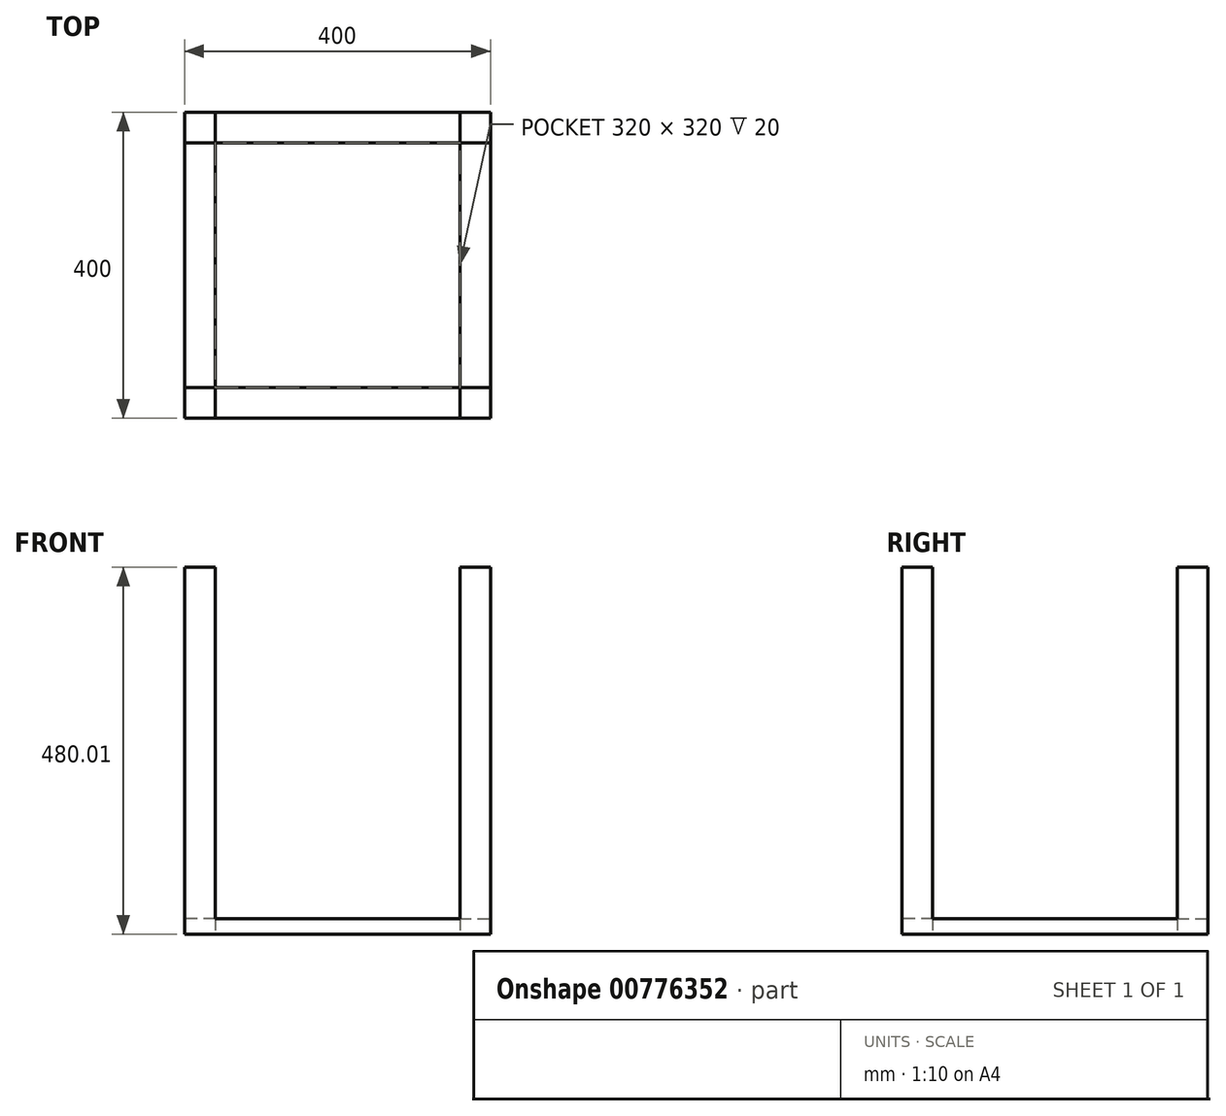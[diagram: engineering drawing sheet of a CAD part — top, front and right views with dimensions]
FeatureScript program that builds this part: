
annotation { "Feature Type Name" : "Feature", "Feature Type Description" : "" }
export const myFeature = defineFeature(function(context is Context, id is Id, definition is map)
    precondition{}
    {
        {
            var Q0;
            Q0=qCreatedBy(makeId("Top.planeOp"),FACE);
            var sketch = newSketch(context, id + "F0", { "sketchPlane" : qUnion([Q0])});
            skLineSegment(sketch, "E0.bottom", {"start": v(0, 0) * mm, "end": v(400, 0) * mm});
            skLineSegment(sketch, "E0.top", {"start": v(0, 400) * mm, "end": v(400, 400) * mm});
            skLineSegment(sketch, "E0.left", {"start": v(0, 0) * mm, "end": v(0, 400) * mm});
            skLineSegment(sketch, "E0.right", {"start": v(400, 0) * mm, "end": v(400, 400) * mm});
            skSolve(sketch);
        }
        {
            var Q0;
            Q0 = qSketchRegion(id + "F0", true);
            extrude(context, id + "F1", {"entities" : qUnion([Q0]), "depth" : 1 / 101.6 * mm, "offsetDistance" : 25 * mm});
        }
        {
            var Q0;
            Q0=makeQuery(id+"F1.opExtrude","CAP_FACE",FACE,{"disambiguationData":[OSD([sQuery(id+"F0.wireOp",EDGE,"E0.bottom"),sQuery(id+"F0.wireOp",EDGE,"E0.top"),sQuery(id+"F0.wireOp",EDGE,"E0.left"),sQuery(id+"F0.wireOp",EDGE,"E0.right")])],"isStart":false});
            var sketch = newSketch(context, id + "F2", { "sketchPlane" : qUnion([Q0])});
            skLineSegment(sketch, "E1.bottom", {"start": v(0, 400) * mm, "end": v(400, 400) * mm});
            skLineSegment(sketch, "E1.top", {"start": v(0, 0) * mm, "end": v(400, 0) * mm});
            skLineSegment(sketch, "E1.left", {"start": v(0, 400) * mm, "end": v(0, 0) * mm});
            skLineSegment(sketch, "E1.right", {"start": v(400, 400) * mm, "end": v(400, 0) * mm});
            skLineSegment(sketch, "E2.0", {"start": v(40, 360) * mm, "end": v(360, 360) * mm});
            skLineSegment(sketch, "E2.1", {"start": v(40, 360) * mm, "end": v(40, 40) * mm});
            skLineSegment(sketch, "E2.2", {"start": v(40, 40) * mm, "end": v(360, 40) * mm});
            skLineSegment(sketch, "E2.3", {"start": v(360, 360) * mm, "end": v(360, 40) * mm});
            skSolve(sketch);
        }
        {
            var Q0;
            Q0 = qSketchRegion(id + "F2", true);
            extrude(context, id + "F3", {"entities" : qUnion([Q0]), "operationType" : NewBodyOperationType.ADD, "depth" : 20 * mm, "offsetDistance" : 25 * mm});
        }
        {
            var Q0;
            Q0=makeQuery(id+"F3.opExtrude","CAP_FACE",FACE,{"disambiguationData":[OSD([sQuery(id+"F2.wireOp",EDGE,"E1.bottom"),sQuery(id+"F2.wireOp",EDGE,"E1.top"),sQuery(id+"F2.wireOp",EDGE,"E1.left"),sQuery(id+"F2.wireOp",EDGE,"E1.right"),sQuery(id+"F2.wireOp",EDGE,"E2.0"),sQuery(id+"F2.wireOp",EDGE,"E2.1"),sQuery(id+"F2.wireOp",EDGE,"E2.2"),sQuery(id+"F2.wireOp",EDGE,"E2.3")])],"isStart":false});
            var sketch = newSketch(context, id + "F4", { "sketchPlane" : qUnion([Q0])});
            skLineSegment(sketch, "E3.bottom", {"start": v(40, 360) * mm, "end": v(0, 360) * mm});
            skLineSegment(sketch, "E3.top", {"start": v(40, 400) * mm, "end": v(0, 400) * mm});
            skLineSegment(sketch, "E3.left", {"start": v(40, 360) * mm, "end": v(40, 400) * mm});
            skLineSegment(sketch, "E3.right", {"start": v(0, 360) * mm, "end": v(0, 400) * mm});
            skLineSegment(sketch, "E4.bottom", {"start": v(360, 360) * mm, "end": v(400, 360) * mm});
            skLineSegment(sketch, "E4.top", {"start": v(360, 400) * mm, "end": v(400, 400) * mm});
            skLineSegment(sketch, "E4.left", {"start": v(360, 360) * mm, "end": v(360, 400) * mm});
            skLineSegment(sketch, "E4.right", {"start": v(400, 360) * mm, "end": v(400, 400) * mm});
            skLineSegment(sketch, "E5.bottom", {"start": v(360, 40) * mm, "end": v(400, 40) * mm});
            skLineSegment(sketch, "E5.top", {"start": v(360, 0) * mm, "end": v(400, 0) * mm});
            skLineSegment(sketch, "E5.left", {"start": v(360, 40) * mm, "end": v(360, 0) * mm});
            skLineSegment(sketch, "E5.right", {"start": v(400, 40) * mm, "end": v(400, 0) * mm});
            skLineSegment(sketch, "E6.bottom", {"start": v(40, 40) * mm, "end": v(0, 40) * mm});
            skLineSegment(sketch, "E6.top", {"start": v(40, 0) * mm, "end": v(0, 0) * mm});
            skLineSegment(sketch, "E6.left", {"start": v(40, 40) * mm, "end": v(40, 0) * mm});
            skLineSegment(sketch, "E6.right", {"start": v(0, 40) * mm, "end": v(0, 0) * mm});
            skSolve(sketch);
        }
        {
            var Q0;
            Q0 = qSketchRegion(id + "F4", true);
            extrude(context, id + "F5", {"entities" : qUnion([Q0]), "operationType" : NewBodyOperationType.ADD, "depth" : (500 - 40) * mm, "offsetDistance" : 25 * mm});
        }
    });
